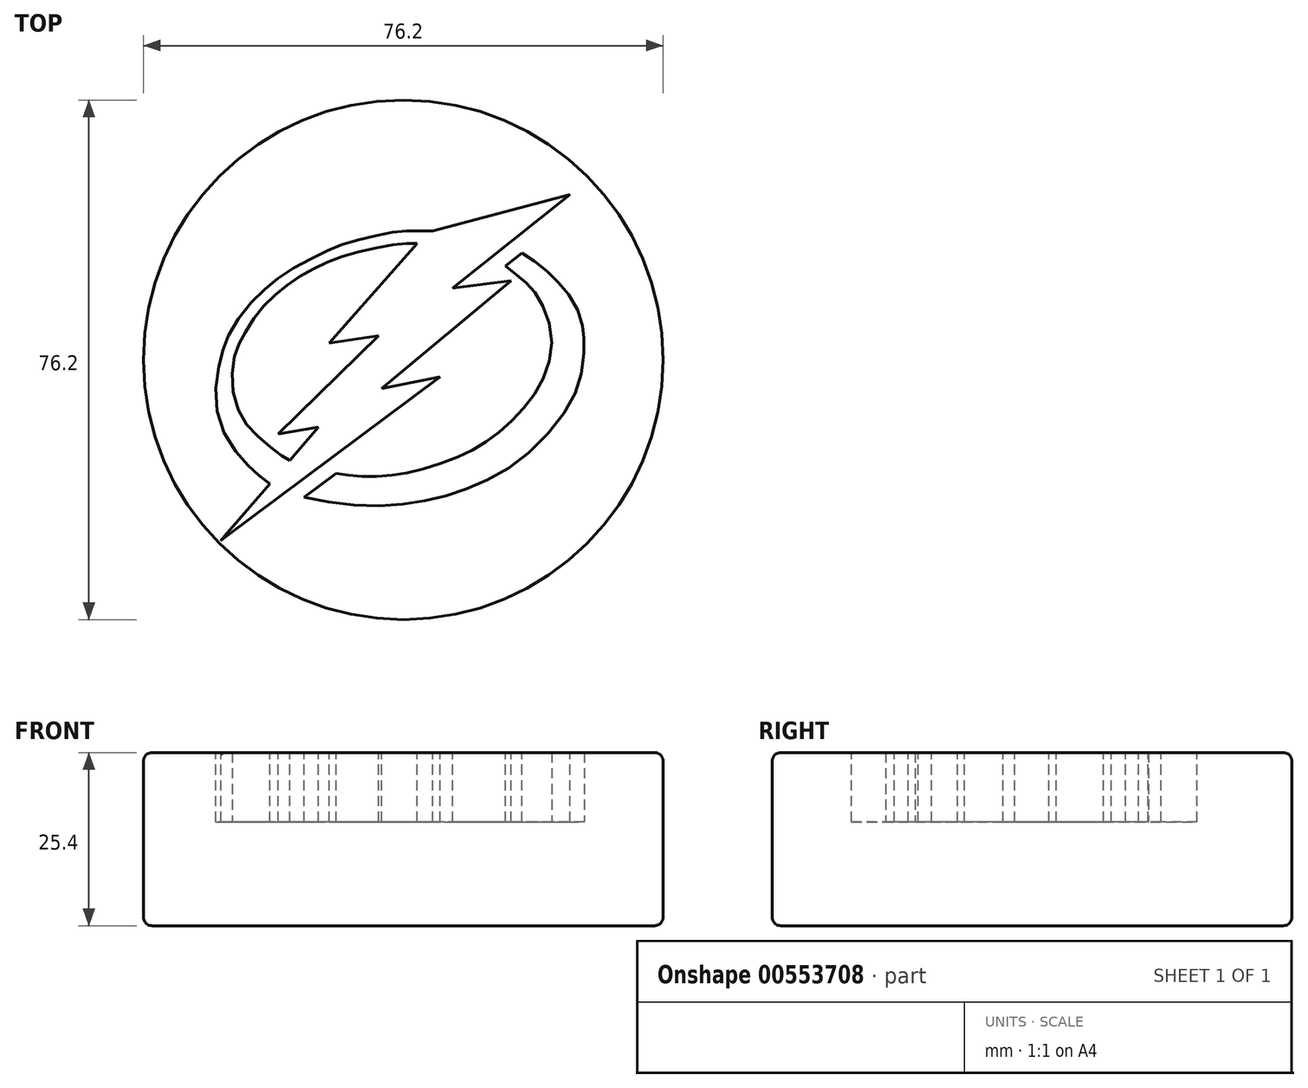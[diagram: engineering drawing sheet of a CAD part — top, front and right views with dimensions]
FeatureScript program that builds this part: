
annotation { "Feature Type Name" : "Feature", "Feature Type Description" : "" }
export const myFeature = defineFeature(function(context is Context, id is Id, definition is map)
    precondition{}
    {
        {
            var Q0;
            Q0=qCreatedBy(makeId("Top.planeOp"),FACE);
            var sketch = newSketch(context, id + "F0", { "sketchPlane" : qUnion([Q0])});
            skCircle(sketch, "E0", {"center": v(0, 0) * mm, "radius": 38.1 * mm});
            skSolve(sketch);
        }
        {
            var Q0;
            Q0 = qSketchRegion(id + "F0", true);
            extrude(context, id + "F1", {"entities" : qUnion([Q0]), "depth" : 25.4 * mm, "offsetDistance" : 25.4 * mm});
        }
        {
            var Q0;
            Q0=makeQuery(id+"F1.opExtrude","CAP_EDGE",EDGE,{"disambiguationData":[OSD([sQuery(id+"F0.wireOp",EDGE,"E0")])],"isStart":false});
            var Q1;
            Q1=makeQuery(id+"F1.opExtrude","CAP_EDGE",EDGE,{"disambiguationData":[OSD([sQuery(id+"F0.wireOp",EDGE,"E0")])],"isStart":true});
            fillet(context, id + "F2", {"entities" : qUnion([Q0, Q1]), "radius" : 1.27 * mm, "tangentPropagation" : true, "allowEdgeOverflow" : false});
        }
        {
            var Q0;
            Q0=makeQuery(id+"F1.opExtrude","CAP_FACE",FACE,{"disambiguationData":[OSD([sQuery(id+"F0.wireOp",EDGE,"E0")])],"isStart":false});
            var sketch = newSketch(context, id + "F3", { "sketchPlane" : qUnion([Q0])});
            skLineSegment(sketch, "E1", {"start": v(-26.76, -26.49) * mm, "end": v(5.4, -2.51) * mm});
            skLineSegment(sketch, "E2", {"start": v(5.4, -2.51) * mm, "end": v(-3.2, -4.24) * mm});
            skLineSegment(sketch, "E3", {"start": v(-3.2, -4.24) * mm, "end": v(15.84, 11.6) * mm});
            skLineSegment(sketch, "E4", {"start": v(15.84, 11.6) * mm, "end": v(7.26, 10.48) * mm});
            skLineSegment(sketch, "E5", {"start": v(7.26, 10.48) * mm, "end": v(24.43, 24.21) * mm});
            skLineSegment(sketch, "E6", {"start": v(24.43, 24.21) * mm, "end": v(4.3, 18.9) * mm});
            skLineSegment(sketch, "E7", {"start": v(2.04, 17.03) * mm, "end": v(-10.9, 2.46) * mm});
            skLineSegment(sketch, "E8", {"start": v(-10.9, 2.46) * mm, "end": v(-3.6, 3.54) * mm});
            skLineSegment(sketch, "E9", {"start": v(-3.6, 3.54) * mm, "end": v(-18.36, -10.9) * mm});
            skLineSegment(sketch, "E10", {"start": v(-19.57, -18.17) * mm, "end": v(-26.76, -26.49) * mm});
            skFitSpline(sketch, "E11", {"points": [v(2.04, 17.03) * mm, v(0, 17.03) * mm, v(-3.48, 16.52) * mm, v(-8.46, 15.29) * mm, v(-12.2, 13.8) * mm, v(-15.63, 11.93) * mm, v(-18.66, 9.6) * mm, v(-21.31, 6.9) * mm, v(-23.44, 3.53) * mm, v(-24.6, 1.01) * mm, v(-25.06, -3.7) * mm, v(-23.57, -8.61) * mm, v(-20.73, -11.78) * mm, v(-17.82, -14.04) * mm, v(-16.66, -14.75) * mm], "startDerivative": vector(-36.01, 1.35) * mm, "endDerivative": vector(23.74, -13.42) * mm});
            skLineSegment(sketch, "E12", {"start": v(-16.66, -14.75) * mm, "end": v(-12.42, -9.9) * mm});
            skLineSegment(sketch, "E13", {"start": v(-12.42, -9.9) * mm, "end": v(-18.36, -10.9) * mm});
            skLineSegment(sketch, "E14", {"start": v(17.39, 15.63) * mm, "end": v(15, 13.75) * mm});
            skFitSpline(sketch, "E15", {"points": [v(-9.85, -16.67) * mm, v(-6.7, -17.08) * mm, v(-2.41, -17) * mm, v(1.96, -16.24) * mm, v(8.18, -14.18) * mm, v(12.38, -11.87) * mm, v(16.58, -8.3) * mm, v(20.07, -3.63) * mm, v(21.75, 2.72) * mm, v(19.9, 8.98) * mm, v(17.72, 11.54) * mm, v(15, 13.75) * mm], "startDerivative": vector(40.99, -6.8) * mm, "endDerivative": vector(-36.77, 28.68) * mm});
            skFitSpline(sketch, "E16", {"points": [v(17.39, 15.63) * mm, v(19.33, 14.43) * mm, v(21.29, 12.78) * mm, v(23.01, 11) * mm, v(24.69, 8.88) * mm, v(26.07, 5.97) * mm, v(26.4, 3.93) * mm, v(26.5, 2.75) * mm, v(26.35, -0.6) * mm, v(25.3, -4.71) * mm, v(22.38, -9.4) * mm, v(17.39, -14.49) * mm, v(12.25, -17.64) * mm, v(7.51, -19.6) * mm, v(3.14, -20.68) * mm, v(-2.09, -21.36) * mm, v(-8.3, -21.23) * mm, v(-14.54, -20.17) * mm], "startDerivative": vector(43.48, -25.06) * mm, "endDerivative": vector(-83.04, 16.93) * mm});
            skFitSpline(sketch, "E17", {"points": [v(4.3, 18.9) * mm, v(2.85, 18.9) * mm, v(0.18, 18.9) * mm, v(-2.41, 18.54) * mm, v(-6.38, 17.62) * mm, v(-9.66, 16.63) * mm, v(-12.53, 15.33) * mm, v(-16.76, 13) * mm, v(-19.86, 10.71) * mm, v(-22.8, 7.8) * mm, v(-25.66, 3.53) * mm, v(-26.57, 1.01) * mm, v(-27.46, -3.7) * mm, v(-26.58, -10.06) * mm, v(-23.57, -14.64) * mm, v(-21.31, -16.82) * mm, v(-19.57, -18.17) * mm], "startDerivative": vector(-33.34, -0.33) * mm, "endDerivative": vector(35.42, -26.34) * mm});
            skLineSegment(sketch, "E18", {"start": v(-9.85, -16.67) * mm, "end": v(-14.54, -20.17) * mm});
            skSolve(sketch);
        }
        {
            var Q0;
            Q0 = qSketchRegion(id + "F3", true);
            extrude(context, id + "F4", {"entities" : qUnion([Q0]), "operationType" : NewBodyOperationType.REMOVE, "oppositeDirection" : true, "depth" : 10.16 * mm, "offsetDistance" : 25.4 * mm});
        }
    });
